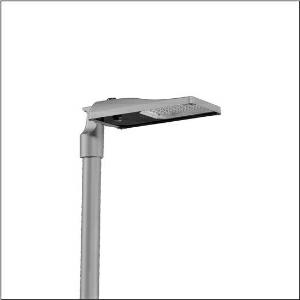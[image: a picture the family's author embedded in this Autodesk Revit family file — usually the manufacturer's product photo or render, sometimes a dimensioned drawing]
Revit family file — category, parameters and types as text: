
# Revit family: streetlight_sl_31_mini___st1_0a_5xh2d3at08ga_96da
name_source: partatom
category: Lighting Fixtures
units: mm (PartAtom-declared; Revit-internal decimal feet)

## family parameters
Cut with Voids When Loaded = No
Host = Face
Light Source = No
Part Type = Normal
Room Calculation Point = No
Round Connector Dimension = Use Diameter
Shared = No

## types (1)
- --- (1 x LED, 5880 lm, 39.3 W, 3000K)
    Apparent Load = 39 VA
    CIE Flux Codes = 37 72 97 100 100
    Color Rendering = 70
    Color Temperature = 3000K
    Default Elevation = 1800 mm
    Description = Streetlight SL 31 mini D4i mast luminaire for post-top, side-entry; light control with lens of PMMA; light distribution: ST1.0a, direct asymmetric distribution, for standard-compliant lighting for roads and squares; LED: luminous flux: 5.880lm, light colour: 730, colour temperature: 3000K; luminous efficacy: 149,6lm/W; control: pre-setting: logarithmic dimming characteristic, flexible luminous flux parameterisation, time-dependent luminous flux control, constant luminous flux control, power reduction, intelligent temperature release in ECG and LED module, overheat protection; luminaire housing, of diecast aluminium, SITECO metallic grey (DB 702S), corrosivity category C5 high according to DIN EN ISO 12944; cover of toughened safety glass, transparent, mast flange of diecast aluminium, SITECO metallic grey (DB 702S), spigot size: 76/60mm, mast flange included unmounted; cable length: 6,5m, connection cable pre-assembled; mains connection: 220..240V, AC, 50/60Hz; power consumption (at start of service life): 39,3W / (at end of service life): 40,7W / (with reduced operation 50%): 18,1W; protection rating (complete): IP66; insulation class (complete): insulation class II (safety insulation); impact resistance: IK09; certification: CE, ENEC, ENEC+, VDE, UKCA, ZD4i; permissible operating ambient temperature for outdoor applications: -40..+50°C; packaging unit: 1 piece

Light Distribution: ST1.0a
    Height = 76 mm
    Lamp = 1 x LED
    Lamp Light Flux = 5880 lm
    Lamp Power = 39.3 W
    Lamp count = 1
    Length = 547 mm
    Luminous efficacy = 150 lm/W
    Manufacturer = Siteco
    ModVariant = No
    Model = 5XH2D3AT08GA
    Number of Poles = 1
    OnlyDefault = Yes
    Power Factor = 1
    Product Name = Streetlight SL 31 mini | ST1.0a
    Product group = mast luminaire | pylon top
    ProductGroupID = 6100
    Protection Class = Protection class II
    Protection Degree = IP 66
    RLX_Detail_Level = 1
    RLX_Emergency_Light_Flux = 0 lm
    RLX_Emergency_Type = 0
    RLX_Emergency_Type_DB = No
    RlxData = <blob elided: 39853 chars, md5=e69e8cc4>
    Socket = socket
    Standby Power = 0 W
    System Light Flux = 5880 lm
    System Power = 39 W
    Type Comments = factory setting: luminous flux: 100 % | dim-lin: 254 | 798 mA
    Type Image = l_1300332.jpg
    URL = http://relux.com
    VarID = @adj_061373
    Voltage = 0 V
    Weight = 0.00 kg
    Width = 265 mm

## geometry (parser evidence)
native form markers: Blend x4, Sweep x9
no freeform markers — native parametric forms only
